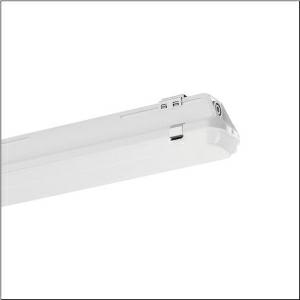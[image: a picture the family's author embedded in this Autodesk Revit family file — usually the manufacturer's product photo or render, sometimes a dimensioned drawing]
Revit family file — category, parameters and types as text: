
# Revit family: monsun_21_51fb10ml660k
name_source: partatom
category: Lighting Fixtures
units: mm (PartAtom-declared; Revit-internal decimal feet)

## family parameters
Cut with Voids When Loaded = No
Host = Face
Light Source = No
Part Type = Normal
Room Calculation Point = No
Round Connector Dimension = Use Diameter
Shared = No

## types (1)
- --- (1 x LED, 5960 lm, 34.1 W, 6500K)
    Apparent Load = 34 VA
    CIE Flux Codes = 46 76 93 94 100
    Color Rendering = 80
    Color Temperature = 6500K
    Default Elevation = 1800 mm
    Description = Monsun 21, damp-proof luminaire, chain hanger, primary optical cover: enclosure, of PMMA, light emission: direct distribution, primary light characteristic: symmetric, installation type: suspended mounting, surface-mounted, horizontal mounting, vertical mounting, LED, rated luminous flux: 5.960lm, luminous efficacy: 175lm/W, light colour: 865, colour temperature: 6500K, control gear: ON/OFF Multilumen, with terminal, 3-pole, max. 2.5mm², mains connection: 220..240V, AC, 50/60Hz, rated input power: 34W, housing, of glass-fibre reinforced plastic, uncoated, bright grey, incl. chain hanger, length: 1.299mm, width: 90mm, height: 88mm, clip for enclosure, of stainless steel (V2A), ceiling mounting element, of stainless steel (V2A), chain hanger, of stainless steel (V2A), protection rating (complete): IP66, insulation class (complete): insulation class I (protective earthing), certification: CE, ENEC, VDE, UKCA, protection symbol: D, impact resistance: IK04, permissible operating ambient temperature: -25..+35°C, standard: EN 50419, EN 60598-2-1, corresponds to IFS (International Featured Standards) requirements for safety and quality in the food industry, for indoor or canopied outdoor use, no direct snow, no direct sun, no direct rain, LABS conformity tested according to VDMA 24364:2018-05, contact your sales advisor before using the luminaires in applications with unclear chemical exposure, large temperature fluctuations or condensation-forming humidity, packaging unit: 1 piece
    Height = 88 mm
    Lamp = 1 x LED
    Lamp Light Flux = 5960 lm
    Lamp Power = 34.1 W
    Lamp count = 1
    Length = 1299 mm
    Luminous efficacy = 175 lm/W
    Manufacturer = Siteco
    ModVariant = No
    Model = 51FB10ML660K
    Mounting Place = Ceiling
    Mounting Type = Surface mounted
    Number of Poles = 1
    OnlyDefault = Yes
    Power Factor = 1
    Product Name = Monsun 21
    Product group = damp-proof luminaire
    ProductGroupID = 300
    Protection Class = Protection class I
    Protection Degree = IP 66
    RLX_Detail_Level = 1
    RLX_Emergency_Light_Flux = 0 lm
    RLX_Emergency_Type = 0
    RLX_Emergency_Type_DB = No
    RlxData = <blob elided: 90933 chars, md5=bed3cc6e>
    Socket = socket
    Standby Power = 0 W
    System Light Flux = 5960 lm
    System Power = 34 W
    Type Comments = factory setting: luminous flux: 100 % | (A | C | E) | 79 mA
    Type Image = l_1319656.jpg
    URL = http://relux.com
    VarID = @adj_049601
    Voltage = 0 V
    Weight = 0.00 kg
    Width = 90 mm

## geometry (parser evidence)
native form markers: Blend x4, Sweep x12
no freeform markers — native parametric forms only
